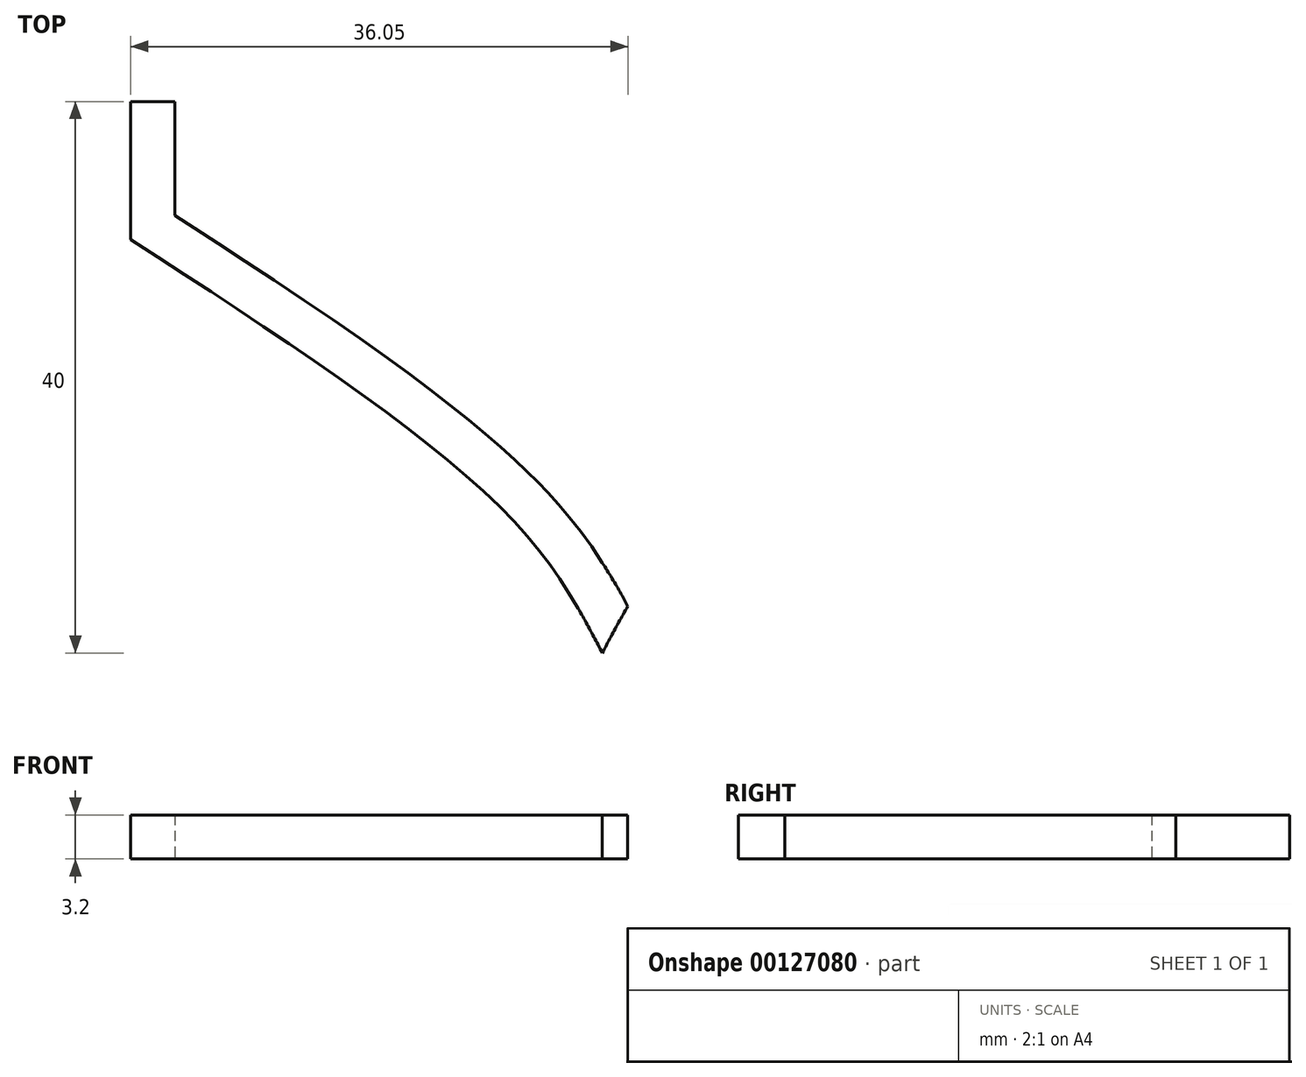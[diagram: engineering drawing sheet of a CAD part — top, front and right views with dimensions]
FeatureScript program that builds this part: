
annotation { "Feature Type Name" : "Feature", "Feature Type Description" : "" }
export const myFeature = defineFeature(function(context is Context, id is Id, definition is map)
    precondition{}
    {
        {
            var Q0;
            Q0=qCreatedBy(makeId("Top.planeOp"),FACE);
            var sketch = newSketch(context, id + "F0", { "sketchPlane" : qUnion([Q0])});
            skLineSegment(sketch, "E0", {"start": v(0, 43.97) * mm, "end": v(0, 0) * mm, "construction": true});
            skLineSegment(sketch, "E1", {"start": v(-6.84, 0) * mm, "end": v(-6.84, -52.59) * mm, "construction": true});
            skLineSegment(sketch, "E2", {"start": v(6.84, 0) * mm, "end": v(6.84, -53.76) * mm, "construction": true});
            skLineSegment(sketch, "E3", {"start": v(-6.84, 0) * mm, "end": v(-6.84, -20) * mm, "construction": true});
            skLineSegment(sketch, "E4", {"start": v(6.84, 0) * mm, "end": v(6.84, -20) * mm, "construction": true});
            skFitSpline(sketch, "E5", {"points": [v(-34.2, 0) * mm, v(-6.84, -20) * mm, v(0, -30) * mm], "startDerivative": vector(51.68, -33.6) * mm, "endDerivative": vector(13.52, -25.75) * mm});
            skFitSpline(sketch, "E6", {"points": [v(34.2, 0) * mm, v(6.84, -20) * mm, v(0, -30) * mm], "startDerivative": vector(-51.68, -33.6) * mm, "endDerivative": vector(-13.52, -25.75) * mm});
            skFitSpline(sketch, "E7.0", {"points": [v(-32.46, 2.68) * mm, v(-30.3, 1.28) * mm, v(-25.99, -1.52) * mm, v(-19.72, -5.7) * mm, v(-14.85, -9.13) * mm, v(-11.3, -11.83) * mm, v(-8.81, -13.82) * mm, v(-6.93, -15.47) * mm, v(-5.54, -16.77) * mm, v(-4.56, -17.75) * mm, v(-3.64, -18.72) * mm, v(-2.53, -20) * mm, v(-1.3, -21.57) * mm, v(-0.04, -23.4) * mm, v(1.4, -25.77) * mm, v(2.27, -27.44) * mm, v(2.83, -28.51) * mm]});
            skFitSpline(sketch, "E8.0", {"points": [v(32.46, 2.68) * mm, v(30.3, 1.28) * mm, v(25.99, -1.52) * mm, v(19.72, -5.7) * mm, v(14.85, -9.13) * mm, v(11.3, -11.83) * mm, v(8.81, -13.82) * mm, v(6.93, -15.47) * mm, v(5.54, -16.77) * mm, v(4.56, -17.75) * mm, v(3.64, -18.72) * mm, v(2.53, -20) * mm, v(1.3, -21.57) * mm, v(0.04, -23.4) * mm, v(-1.4, -25.77) * mm, v(-2.27, -27.44) * mm, v(-2.83, -28.51) * mm]});
            skLineSegment(sketch, "E9", {"start": v(-31, 0) * mm, "end": v(-31, 10) * mm, "construction": true});
            skLineSegment(sketch, "E10", {"start": v(31, 0) * mm, "end": v(31, 10) * mm, "construction": true});
            skLineSegment(sketch, "E11", {"start": v(-34.2, 0) * mm, "end": v(-34.2, 10) * mm});
            skLineSegment(sketch, "E12", {"start": v(34.2, 0) * mm, "end": v(34.2, 10) * mm});
            skLineSegment(sketch, "E13", {"start": v(-34.2, 10) * mm, "end": v(-31, 10) * mm});
            skLineSegment(sketch, "E14", {"start": v(-31, 10) * mm, "end": v(-31, 0) * mm});
            skLineSegment(sketch, "E15", {"start": v(-31, 0) * mm, "end": v(-28.34, 0) * mm});
            skLineSegment(sketch, "E16", {"start": v(34.2, 10) * mm, "end": v(31, 10) * mm});
            skLineSegment(sketch, "E17", {"start": v(31, 10) * mm, "end": v(31, 0) * mm});
            skLineSegment(sketch, "E18.trimOffspring", {"start": v(28.34, 0) * mm, "end": v(31, 0) * mm});
            skLineSegment(sketch, "E19.trimOffspring", {"start": v(-28.34, 0) * mm, "end": v(-31, 0) * mm});
            skLineSegment(sketch, "E20.trimOffspring", {"start": v(0, -30) * mm, "end": v(0, -51.8) * mm, "construction": true});
            skSolve(sketch);
        }
        {
            var Q0;
            {var subQ1=sQuery(id+"F0.wireOp",EDGE,"E6");Q0=makeQuery(id+"F0.imprint","IMPRINT",FACE,{"disambiguationData":[TD([[makeQuery(id+"F0.imprint","IMPRINT",EDGE,{"derivedFrom":subQ1}),-1.0]])]});}
            var Q1;
            {var subQ0=sQuery(id+"F0.wireOp",EDGE,"E11");Q1=makeQuery(id+"F0.imprint","IMPRINT",FACE,{"disambiguationData":[TD([[makeQuery(id+"F0.imprint","IMPRINT",EDGE,{"derivedFrom":subQ0}),-1.0]])]});}
            var Q2;
            {var subQ3=sQuery(id+"F0.wireOp",EDGE,"E5");Q2=makeQuery(id+"F0.imprint","IMPRINT",FACE,{"disambiguationData":[TD([[makeQuery(id+"F0.imprint","IMPRINT",EDGE,{"derivedFrom":subQ3}),1.0]])]});}
            extrude(context, id + "F1", {"entities" : qUnion([Q0, Q1, Q2]), "endBound" : BoundingType.SYMMETRIC, "depth" : 3.2 * mm});
        }
    });
